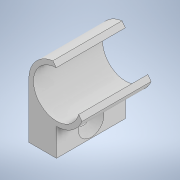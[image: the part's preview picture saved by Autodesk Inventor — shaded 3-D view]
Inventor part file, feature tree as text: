
AUTODESK INVENTOR PART (.ipt)
format: ipt  version: 2021.2 (Build 252289000, 289)  size: 185,856 bytes
history: native  units: in
note: dims shown in document units (in); Inventor stores cm internally (conversion verified against a paired STEP export)
features: sketch x4, extrude x3, hole x1
ambient origin geometry x8: Origin, YZ Plane, XZ Plane, XY Plane, X Axis, Y Axis, Z Axis, Center Point
bodies: Body1 (feature_tree)
feature tree (8):
  extrude  "Extrusion3"  Depth=0.05in
  extrude  "Extrusion4"  Depth=0.4in
  hole  "Hole1"  [1 undecoded]
  extrude  "Text"  Depth=0.045in
  sketch  "Sketch4"  dims[d10=0.5in d11=0.05in]
  sketch  "Sketch5"  dims[d12=0.2577in d13=0.4in]
  sketch  "Sketch6"  dims[d14=0.75in d15=0.0in]
  sketch  "Sketch10"  dims[d16=0.3in d17=0.75in d18=0.0in d19=0.138in d20=0.75in d21=0.28in d22=0.25in d23=0.5635in d24=0.29in d25=0.0in d28=0.045in d29=0.0in]
note: 1 required parameter value undecoded (feature->parameter linkage not recoverable at this tier; creation-order binding heuristic only, values carry confidence <= 0.55)
